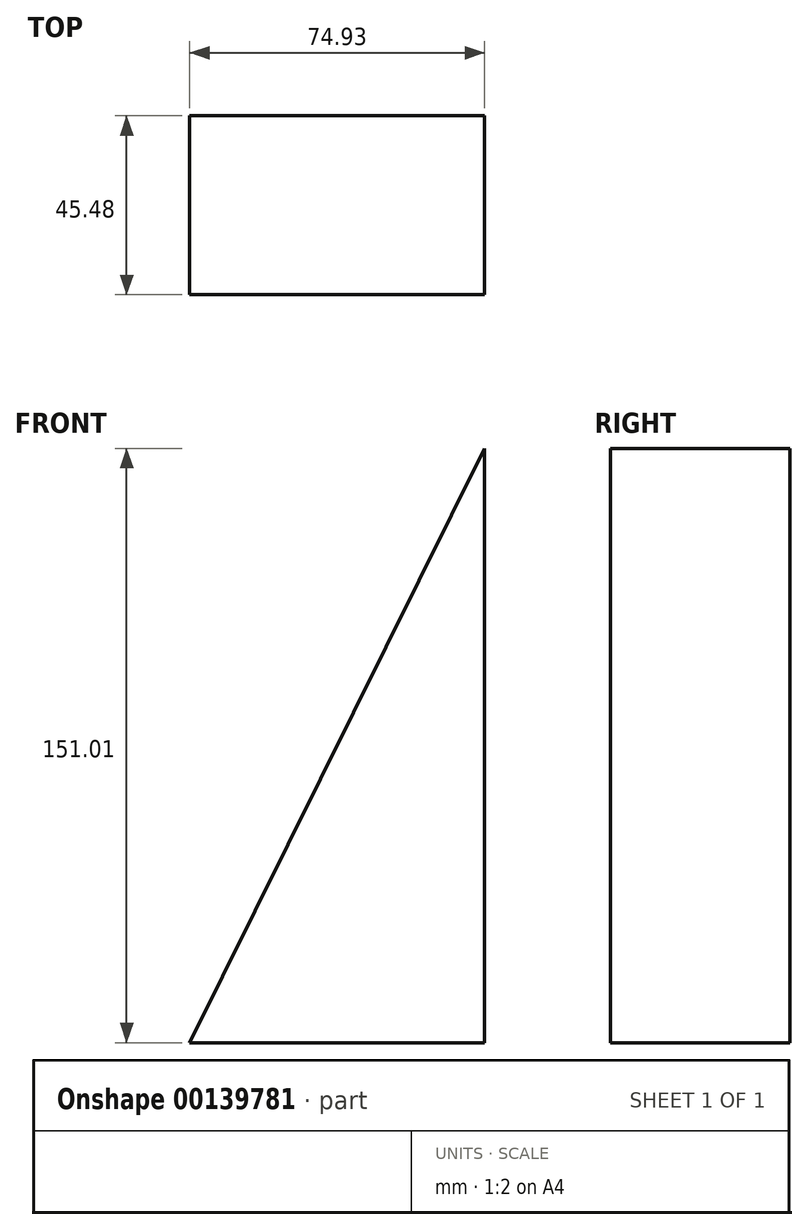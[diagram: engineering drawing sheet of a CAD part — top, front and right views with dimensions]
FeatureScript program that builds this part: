
annotation { "Feature Type Name" : "Feature", "Feature Type Description" : "" }
export const myFeature = defineFeature(function(context is Context, id is Id, definition is map)
    precondition{}
    {
        {
            var Q0;
            Q0=qCreatedBy(makeId("Front.planeOp"),FACE);
            var sketch = newSketch(context, id + "F0", { "sketchPlane" : qUnion([Q0])});
            skLineSegment(sketch, "E0", {"start": v(0, 75.94) * mm, "end": v(-74.93, -75.07) * mm});
            skLineSegment(sketch, "E1", {"start": v(-74.93, -75.07) * mm, "end": v(0, -75.07) * mm});
            skLineSegment(sketch, "E2", {"start": v(0, -75.07) * mm, "end": v(0, 75.94) * mm});
            skSolve(sketch);
        }
        {
            var Q0;
            Q0=makeQuery(id+"F0.imprint","IMPRINT",FACE,{"disambiguationData":[TD([[makeQuery(id+"F0.imprint","IMPRINT",EDGE,{"derivedFrom":sQuery(id+"F0.wireOp",EDGE,"E0")}),1.0]])]});
            extrude(context, id + "F1", {"entities" : qUnion([Q0]), "depth" : 45.48 * mm});
        }
    });
